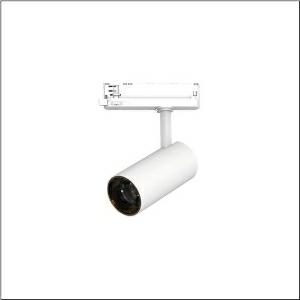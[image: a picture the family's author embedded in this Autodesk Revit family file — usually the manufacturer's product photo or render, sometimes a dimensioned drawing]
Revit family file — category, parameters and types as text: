
# Revit family: spot_31_slim_51sf137fb2b
name_source: partatom
category: Lighting Fixtures
units: mm (PartAtom-declared; Revit-internal decimal feet)

## family parameters
Cut with Voids When Loaded = No
Host = Face
Light Source = No
Part Type = Normal
Room Calculation Point = No
Round Connector Dimension = Use Diameter
Shared = No

## types (1)
- Spot 31 Slim (1 x LED, 2170 lm, 17.6 W, 3000K)
    Apparent Load = 18 VA
    CIE Flux Codes = 97 100 100 100 100
    Color Rendering = 90
    Color Temperature = 3000K
    Default Elevation = 1800 mm
    Description = Spot 31 Slim, directional spotlight, light control with reflector, of aluminium, LED rated luminous flux: 2.200lm, light colour: 930, control gear: ECG, with 3-phase adapter, mains connection: 220..240V, AC, 50/60Hz, housing, of aluminium, traffic white (RAL 9016), diameter: 70mm, adapter, of plastic, protection rating (complete): IP20, insulation class (complete): insulation class I (protective earthing), certification: CE, impact resistance: IK02, packaging unit: 1 piece
    Height = 210 mm
    Lamp = 1 x LED
    Lamp Light Flux = 2170 lm
    Lamp Power = 17.6 W
    Lamp count = 1
    Length = 70 mm
    Luminous efficacy = 123 lm/W
    Manufacturer = Siteco
    ModVariant = No
    Model = 51SF137FB2B
    Mounting Place = Ceiling
    Mounting Type = Pendant
    Number of Poles = 1
    OnlyDefault = Yes
    Power Factor = 1
    Product Name = Spot 31 Slim
    Product group = directional spotlight
    ProductGroupID = 905
    Protection Class = Protection class I
    Protection Degree = IP 20
    RLX_Detail_Level = 1
    RLX_Emergency_Light_Flux = 0 lm
    RLX_Emergency_Type = 0
    RLX_Emergency_Type_DB = No
    RlxData = <blob elided: 14145 chars, md5=6ac1db7b>
    Socket = socket
    Standby Power = 0 W
    System Light Flux = 2170 lm
    System Power = 18 W
    Type Comments = Product without accessories
    Type Image = l_1228468.jpg
    URL = http://relux.com
    VarID = ---
    Voltage = 0 V
    Weight = 0.00 kg
    Width = 0 mm  [stored 0 ft]

note: [stored X ft] marks values corroborated as IEEE doubles in the binary element streams (Revit-internal decimal feet)

## geometry (parser evidence)
native form markers: Sweep x11
no freeform markers — native parametric forms only
